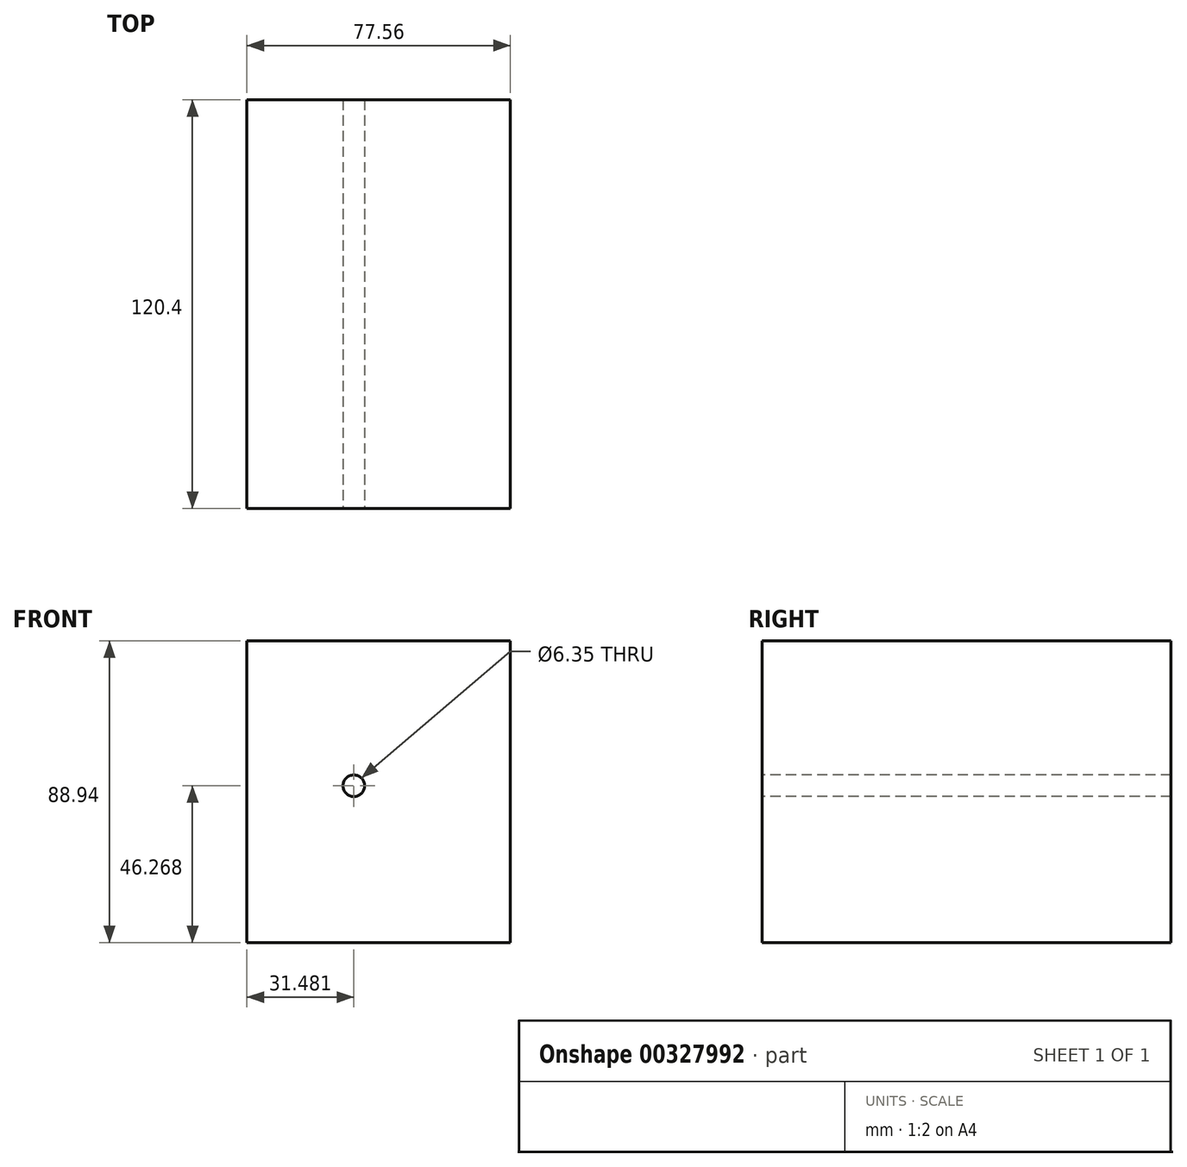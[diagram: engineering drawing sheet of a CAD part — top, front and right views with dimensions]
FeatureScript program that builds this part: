
annotation { "Feature Type Name" : "Feature", "Feature Type Description" : "" }
export const myFeature = defineFeature(function(context is Context, id is Id, definition is map)
    precondition{}
    {
        {
            var Q0;
            Q0=qCreatedBy(makeId("Front.planeOp"),FACE);
            var sketch = newSketch(context, id + "F0", { "sketchPlane" : qUnion([Q0])});
            skLineSegment(sketch, "E0.bottom", {"start": v(0, 0) * mm, "end": v(77.56, 0) * mm});
            skLineSegment(sketch, "E0.top", {"start": v(0, 88.94) * mm, "end": v(77.56, 88.94) * mm});
            skLineSegment(sketch, "E0.left", {"start": v(0, 0) * mm, "end": v(0, 88.94) * mm});
            skLineSegment(sketch, "E0.right", {"start": v(77.56, 0) * mm, "end": v(77.56, 88.94) * mm});
            skSolve(sketch);
        }
        {
            var Q0;
            Q0 = qSketchRegion(id + "F0", true);
            extrude(context, id + "F1", {"entities" : qUnion([Q0]), "depth" : 120.4 * mm});
        }
        {
            var Q0;
            Q0=makeQuery(id+"F1.opExtrude","CAP_FACE",FACE,{"disambiguationData":[OSD([sQuery(id+"F0.wireOp",EDGE,"E0.bottom"),sQuery(id+"F0.wireOp",EDGE,"E0.top"),sQuery(id+"F0.wireOp",EDGE,"E0.left"),sQuery(id+"F0.wireOp",EDGE,"E0.right")])],"isStart":false});
            var sketch = newSketch(context, id + "F2", { "sketchPlane" : qUnion([Q0])});
            skCircle(sketch, "E1", {"center": v(31.48, 46.27) * mm, "radius": 17.61 * mm});
            skSolve(sketch);
        }
        {
            var Q0;
            Q0=sQuery(id+"F2.wireOp",VERTEX,"E1.center");
            var Q1;
            Q1=makeQuery(id+"F1.opExtrude","SWEPT_BODY",BODY,{"disambiguationData":[OSD([sQuery(id+"F0.wireOp",EDGE,"E0.bottom"),sQuery(id+"F0.wireOp",EDGE,"E0.top"),sQuery(id+"F0.wireOp",EDGE,"E0.left"),sQuery(id+"F0.wireOp",EDGE,"E0.right")])]});
            hole(context, id + "F3", {"style" : HoleStyle.SIMPLE, "endStyle" : HoleEndStyle.THROUGH, "holeDiameter" : 6.35 * mm, "tappedDepth" : 12.7 * mm, "tapClearance" : 3, "locations" : qUnion([Q0]), "scope" : qUnion([Q1])});
        }
    });
